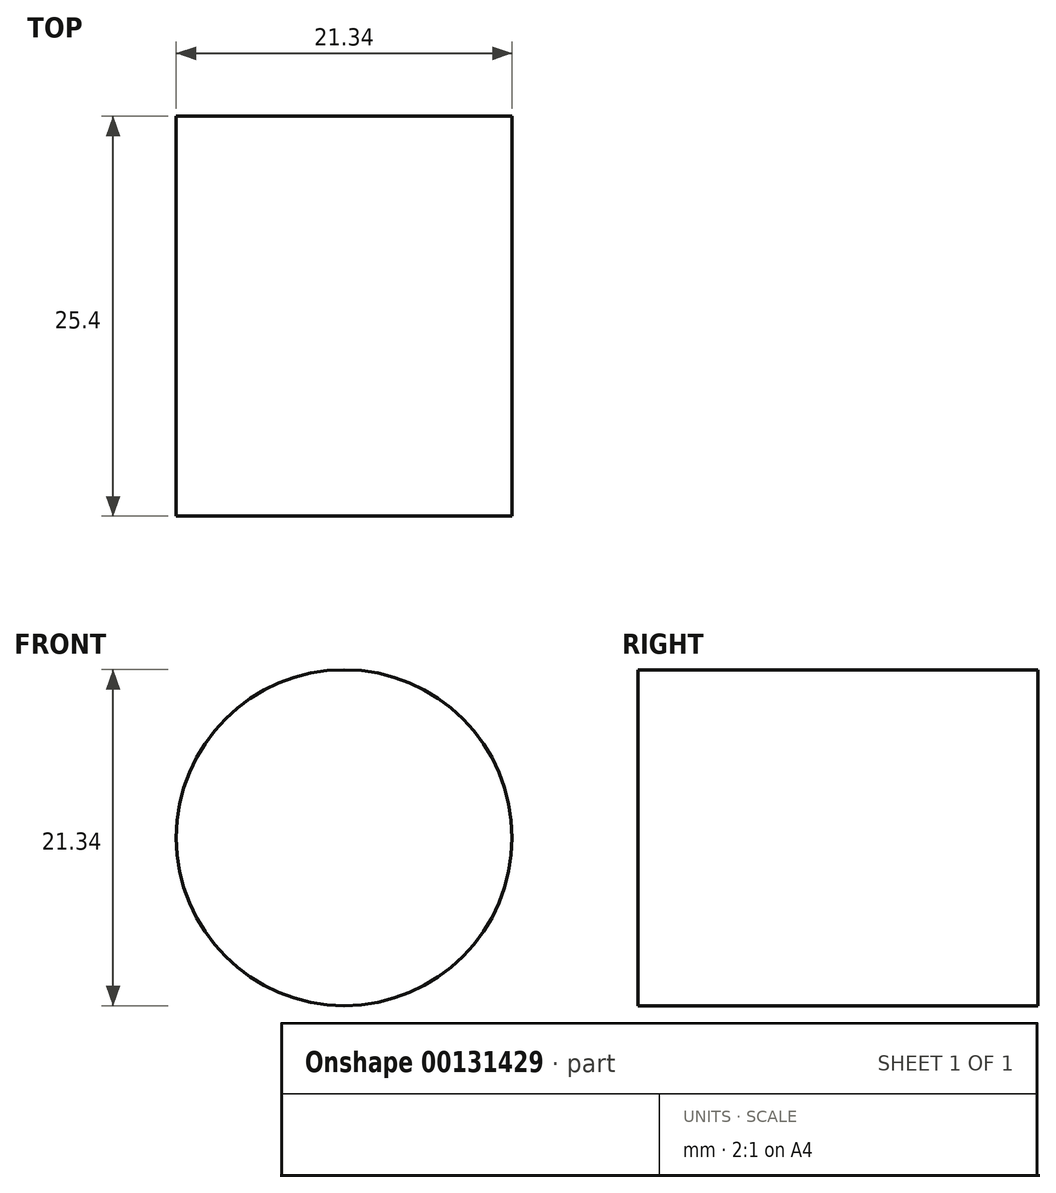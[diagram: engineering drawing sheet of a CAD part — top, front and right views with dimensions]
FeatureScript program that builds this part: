
annotation { "Feature Type Name" : "Feature", "Feature Type Description" : "" }
export const myFeature = defineFeature(function(context is Context, id is Id, definition is map)
    precondition{}
    {
        {
            var Q0;
            Q0=qCreatedBy(makeId("Front.planeOp"),FACE);
            var sketch = newSketch(context, id + "F0", { "sketchPlane" : qUnion([Q0])});
            skCircle(sketch, "E0", {"center": v(0, 0) * mm, "radius": 10.67 * mm});
            skSolve(sketch);
        }
        {
            var Q0;
            Q0=makeQuery(id+"F0.imprint","IMPRINT",FACE,{"disambiguationData":[TD([[makeQuery(id+"F0.imprint","IMPRINT",EDGE,{"derivedFrom":sQuery(id+"F0.wireOp",EDGE,"E0")}),1.0]])]});
            extrude(context, id + "F1", {"entities" : qUnion([Q0]), "depth" : 25.4 * mm});
        }
    });
